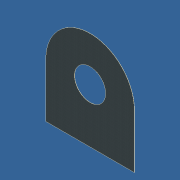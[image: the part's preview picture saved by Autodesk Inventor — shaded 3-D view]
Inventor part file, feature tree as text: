
AUTODESK INVENTOR PART (.ipt)
format: ipt  version: unknown  size: 172,032 bytes
history: native  units: in
note: dims shown in document units (in); Inventor stores cm internally (conversion verified against a paired STEP export)
features: extrude x2, sketch x1
ambient origin geometry x8: Origin, YZ Plane, XZ Plane, XY Plane, X Axis, Y Axis, Z Axis, Center Point
bodies: Solid1 (feature_tree)
feature tree (3):
  sketch  "Sketch1"  dims[d0=86.0in d1=52.5in d2=0.1875in d3=0.0in d4=30.25in d5=1.0in d6=0.0in]
  extrude  "Extrusion1"  Depth=52.5in
  extrude  "Extrusion2"  Depth=0.1875in TaperAngle=0.0deg
